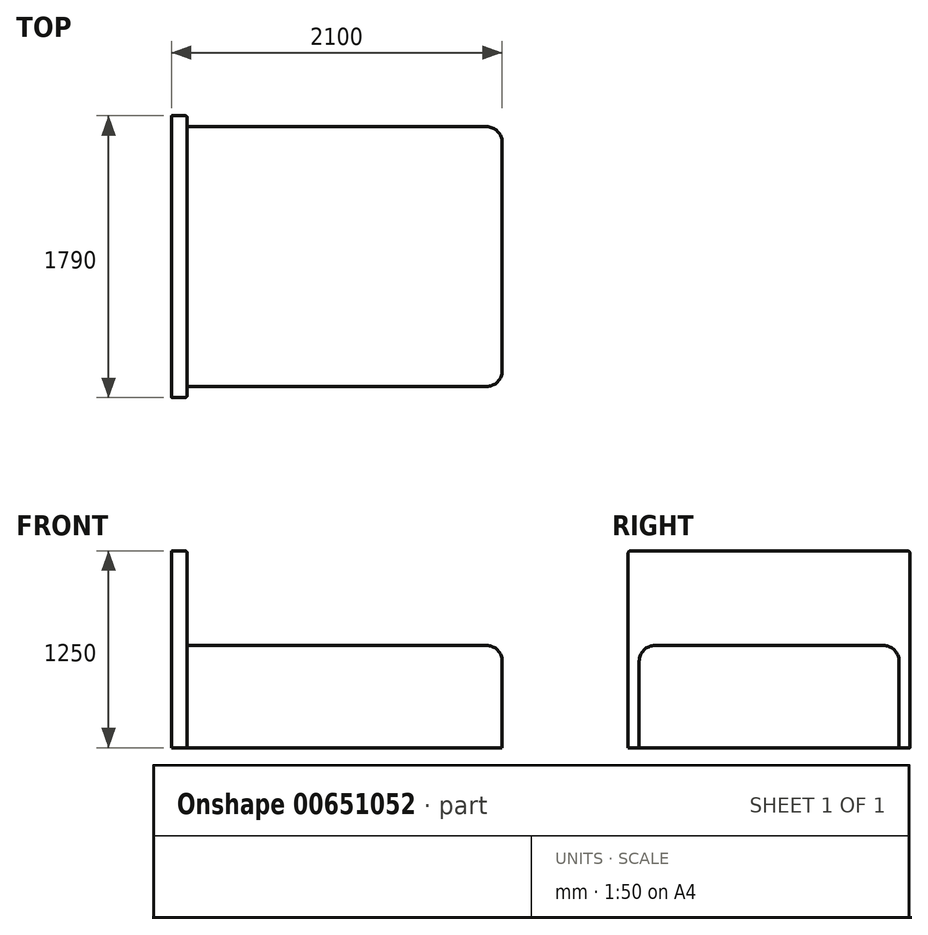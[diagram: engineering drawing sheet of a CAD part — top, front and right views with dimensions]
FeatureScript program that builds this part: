
annotation { "Feature Type Name" : "Feature", "Feature Type Description" : "" }
export const myFeature = defineFeature(function(context is Context, id is Id, definition is map)
    precondition{}
    {
        {
            var Q0;
            Q0=qCreatedBy(makeId("Top.planeOp"),FACE);
            var sketch = newSketch(context, id + "F0", { "sketchPlane" : qUnion([Q0])});
            skLineSegment(sketch, "E0.bottom", {"start": v(0, 0) * mm, "end": v(-2000, 0) * mm});
            skLineSegment(sketch, "E0.top", {"start": v(0, 1650) * mm, "end": v(-2000, 1650) * mm});
            skLineSegment(sketch, "E0.left", {"start": v(0, 0) * mm, "end": v(0, 1650) * mm});
            skLineSegment(sketch, "E0.right", {"start": v(-2000, 0) * mm, "end": v(-2000, 1650) * mm});
            skLineSegment(sketch, "E1.bottom", {"start": v(-2000, 1720) * mm, "end": v(-2100, 1720) * mm});
            skLineSegment(sketch, "E1.top", {"start": v(-2000, -70) * mm, "end": v(-2100, -70) * mm});
            skLineSegment(sketch, "E1.left", {"start": v(-2000, 1720) * mm, "end": v(-2000, -70) * mm});
            skLineSegment(sketch, "E1.right", {"start": v(-2100, 1720) * mm, "end": v(-2100, -70) * mm});
            skSolve(sketch);
        }
        {
            var Q0;
            Q0=makeQuery(id+"F0.imprint","IMPRINT",FACE,{"disambiguationData":[TD([[makeQuery(id+"F0.imprint","IMPRINT",EDGE,{"derivedFrom":sQuery(id+"F0.wireOp",EDGE,"E0.bottom")}),-1.0]])]});
            extrude(context, id + "F1", {"entities" : qUnion([Q0]), "depth" : 650 * mm, "offsetDistance" : 25 * mm});
        }
        {
            var Q0;
            {var subQ1=sQuery(id+"F0.wireOp",EDGE,"E0.right");Q0=makeQuery(id+"F0.imprint","IMPRINT",FACE,{"disambiguationData":[TD([[makeQuery(id+"F0.imprint","IMPRINT",EDGE,{"derivedFrom":subQ1}),1.0]])]});}
            extrude(context, id + "F2", {"entities" : qUnion([Q0]), "operationType" : NewBodyOperationType.ADD, "depth" : 1250 * mm, "offsetDistance" : 25 * mm});
        }
        {
            var Q0;
            Q0=makeQuery(id+"F2.opExtrude","CAP_EDGE",EDGE,{"disambiguationData":[OSD([sQuery(id+"F0.wireOp",EDGE,"E0.right"),sQuery(id+"F0.wireOp",EDGE,"E1.left")])],"isStart":false});
            var Q1;
            Q1=makeQuery(id+"F2.opExtrude","SWEPT_EDGE",EDGE,{"disambiguationData":[OSD([sQuery(id+"F0.wireOp",EDGE,"E1.bottom"),sQuery(id+"F0.wireOp",EDGE,"E1.left")])]});
            var Q2;
            Q2=makeQuery(id+"F2.opExtrude","SWEPT_EDGE",EDGE,{"disambiguationData":[OSD([sQuery(id+"F0.wireOp",EDGE,"E1.top"),sQuery(id+"F0.wireOp",EDGE,"E1.left")])]});
            var Q3;
            Q3=makeQuery(id+"F2.opExtrude","CAP_EDGE",EDGE,{"disambiguationData":[OSD([sQuery(id+"F0.wireOp",EDGE,"E1.top")])],"isStart":false});
            var Q4;
            Q4=makeQuery(id+"F2.opExtrude","CAP_EDGE",EDGE,{"disambiguationData":[OSD([sQuery(id+"F0.wireOp",EDGE,"E1.bottom")])],"isStart":false});
            fillet(context, id + "F3", {"entities" : qUnion([Q0, Q1, Q2, Q3, Q4]), "radius" : 15 * mm, "tangentPropagation" : true, "allowEdgeOverflow" : false});
        }
        {
            var Q0;
            Q0=makeQuery(id+"F1.opExtrude","CAP_EDGE",EDGE,{"disambiguationData":[OSD([sQuery(id+"F0.wireOp",EDGE,"E0.bottom")])],"isStart":false});
            var Q1;
            Q1=makeQuery(id+"F1.opExtrude","CAP_EDGE",EDGE,{"disambiguationData":[OSD([sQuery(id+"F0.wireOp",EDGE,"E0.left")])],"isStart":false});
            var Q2;
            Q2=makeQuery(id+"F1.opExtrude","CAP_EDGE",EDGE,{"disambiguationData":[OSD([sQuery(id+"F0.wireOp",EDGE,"E0.top")])],"isStart":false});
            var Q3;
            Q3=makeQuery(id+"F1.opExtrude","SWEPT_EDGE",EDGE,{"disambiguationData":[OSD([sQuery(id+"F0.wireOp",EDGE,"E0.bottom"),sQuery(id+"F0.wireOp",EDGE,"E0.left")])]});
            var Q4;
            Q4=makeQuery(id+"F1.opExtrude","SWEPT_EDGE",EDGE,{"disambiguationData":[OSD([sQuery(id+"F0.wireOp",EDGE,"E0.top"),sQuery(id+"F0.wireOp",EDGE,"E0.left")])]});
            fillet(context, id + "F4", {"entities" : qUnion([Q0, Q1, Q2, Q3, Q4]), "radius" : 100 * mm, "tangentPropagation" : true, "allowEdgeOverflow" : false});
        }
    });
